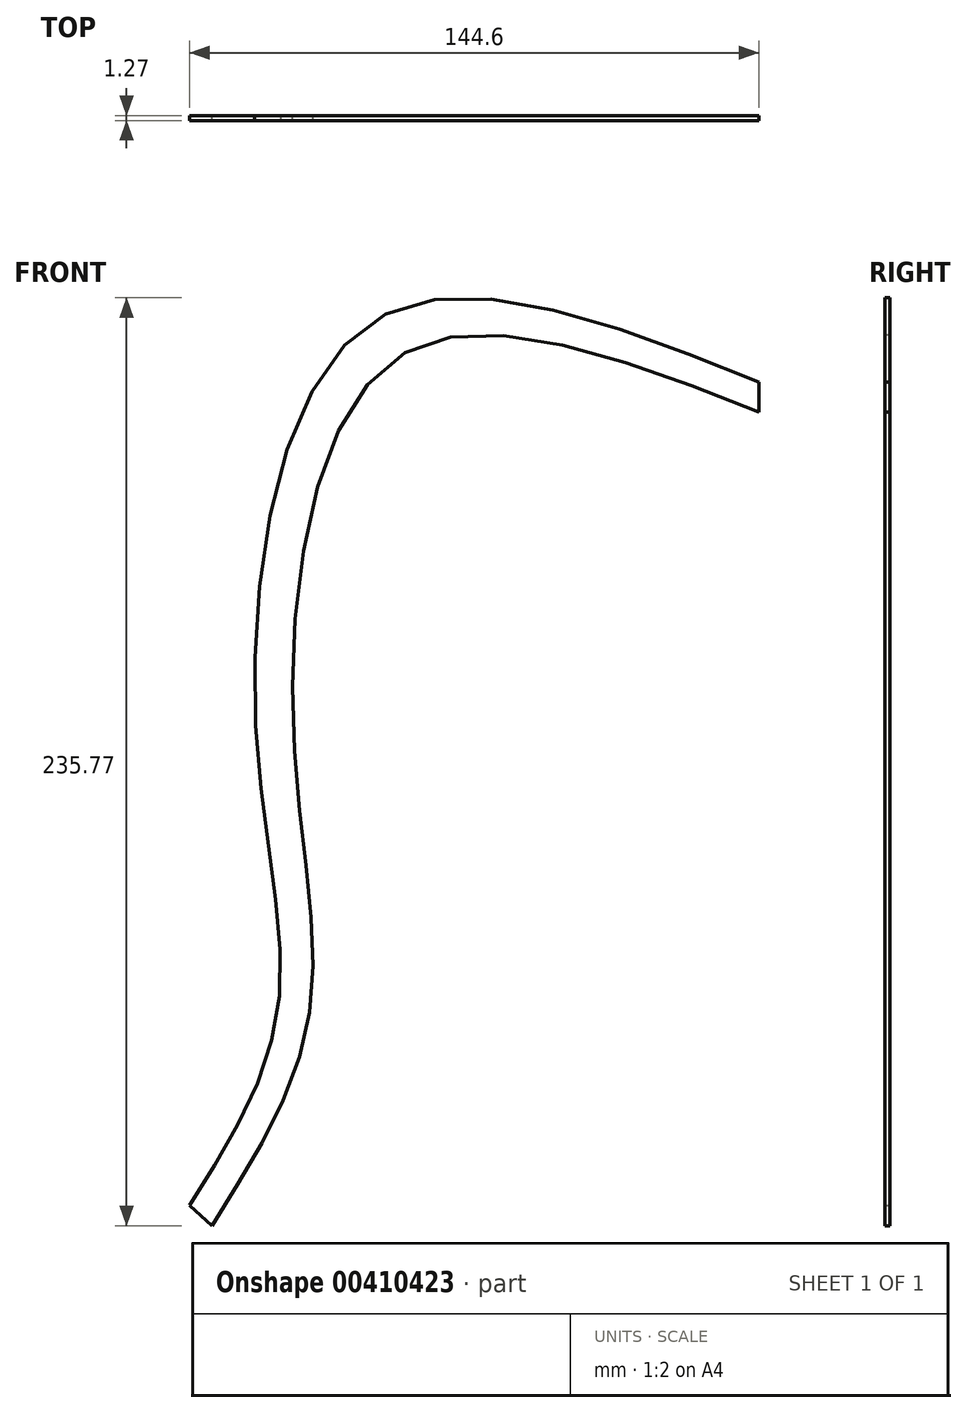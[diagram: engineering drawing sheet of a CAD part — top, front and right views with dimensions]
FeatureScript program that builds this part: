
annotation { "Feature Type Name" : "Feature", "Feature Type Description" : "" }
export const myFeature = defineFeature(function(context is Context, id is Id, definition is map)
    precondition{}
    {
        {
            var Q0;
            Q0=qCreatedBy(makeId("Front.planeOp"),FACE);
            var sketch = newSketch(context, id + "F0", { "sketchPlane" : qUnion([Q0])});
            skFitSpline(sketch, "E0", {"points": [v(0, 0) * mm, v(22.4, 49.58) * mm, v(16.62, 125.72) * mm, v(45.9, 224.34) * mm, v(144.6, 209.29) * mm], "startDerivative": vector(146.86, 234.44) * mm, "endDerivative": vector(413.18, -164.8) * mm});
            skLineSegment(sketch, "E1", {"start": v(144.6, 209.29) * mm, "end": v(144.6, 201.67) * mm});
            skLineSegment(sketch, "E2", {"start": v(0, 0) * mm, "end": v(5.66, -5.1) * mm});
            skFitSpline(sketch, "E3", {"points": [v(5.66, -5.1) * mm, v(30.38, 48.31) * mm, v(26.25, 124.11) * mm, v(52.56, 215.38) * mm, v(144.6, 201.67) * mm], "startDerivative": vector(151.79, 241.17) * mm, "endDerivative": vector(395.65, -154.73) * mm});
            skSolve(sketch);
        }
        {
            var Q0;
            Q0 = qSketchRegion(id + "F0", true);
            extrude(context, id + "F1", {"entities" : qUnion([Q0]), "depth" : 1.27 * mm});
        }
    });
